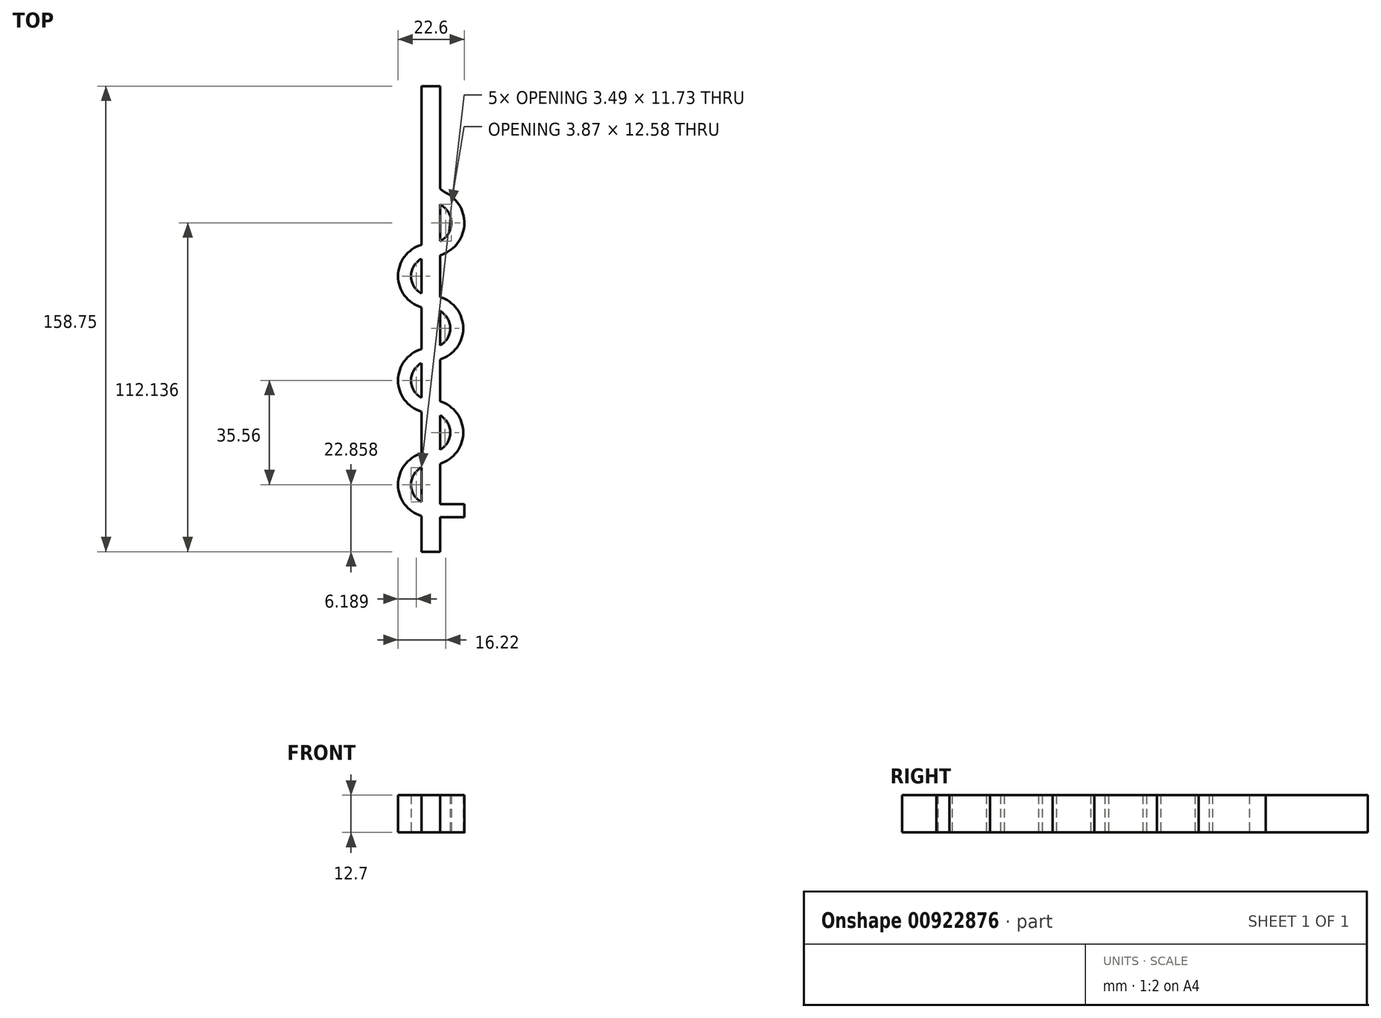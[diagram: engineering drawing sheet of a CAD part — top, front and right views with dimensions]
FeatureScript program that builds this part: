
annotation { "Feature Type Name" : "Feature", "Feature Type Description" : "" }
export const myFeature = defineFeature(function(context is Context, id is Id, definition is map)
    precondition{}
    {
        {
            var Q0;
            Q0=qCreatedBy(makeId("Top.planeOp"),FACE);
            var sketch = newSketch(context, id + "F0", { "sketchPlane" : qUnion([Q0])});
            skLineSegment(sketch, "E0.bottom", {"start": v(-3.18, 89.22) * mm, "end": v(3.17, 89.22) * mm});
            skLineSegment(sketch, "E0.top", {"start": v(-3.18, -69.53) * mm, "end": v(3.17, -69.53) * mm});
            skLineSegment(sketch, "E0.left", {"start": v(-3.18, 89.22) * mm, "end": v(-3.18, -69.53) * mm});
            skLineSegment(sketch, "E0.right", {"start": v(3.17, 89.22) * mm, "end": v(3.17, -69.53) * mm});
            skLineSegment(sketch, "E1", {"start": v(0, 96.84) * mm, "end": v(0, -80.96) * mm, "construction": true});
            skArc(sketch, "E2", {"start": v(0, -40) * mm, "mid": v(-6.67, -46.67) * mm, "end": v(0, -53.34) * mm});
            skArc(sketch, "E3", {"start": v(0, -35.56) * mm, "mid": v(-11.11, -46.67) * mm, "end": v(0, -57.79) * mm});
            skArc(sketch, "E4", {"start": v(0, 0) * mm, "mid": v(-11.11, -11.11) * mm, "end": v(0, -22.23) * mm});
            skArc(sketch, "E5", {"start": v(0, -4.45) * mm, "mid": v(-6.67, -11.11) * mm, "end": v(0, -17.78) * mm});
            skArc(sketch, "E6", {"start": v(0, 35.56) * mm, "mid": v(-11.11, 24.45) * mm, "end": v(0, 13.33) * mm});
            skArc(sketch, "E7", {"start": v(0, 31.12) * mm, "mid": v(-6.67, 24.45) * mm, "end": v(0, 17.78) * mm});
            skArc(sketch, "E8", {"start": v(0, 0) * mm, "mid": v(6.67, 6.67) * mm, "end": v(0, 13.33) * mm});
            skArc(sketch, "E9", {"start": v(0, -4.45) * mm, "mid": v(11.11, 6.67) * mm, "end": v(0, 17.78) * mm});
            skArc(sketch, "E10", {"start": v(0, -35.56) * mm, "mid": v(6.67, -28.9) * mm, "end": v(0, -22.23) * mm});
            skArc(sketch, "E11", {"start": v(0, -40) * mm, "mid": v(11.11, -28.9) * mm, "end": v(0, -17.78) * mm});
            skLineSegment(sketch, "E12", {"start": v(0, -57.78) * mm, "end": v(11.43, -57.78) * mm});
            skLineSegment(sketch, "E13", {"start": v(11.43, -57.78) * mm, "end": v(11.43, -53.34) * mm});
            skLineSegment(sketch, "E14", {"start": v(11.43, -53.34) * mm, "end": v(0, -53.34) * mm});
            skLineSegment(sketch, "E15", {"start": v(-22.23, 48.9) * mm, "end": v(3.17, 48.9) * mm, "construction": true});
            skArc(sketch, "E16", {"start": v(0, 35.56) * mm, "mid": v(6.85, 40.97) * mm, "end": v(3.17, 48.9) * mm});
            skArc(sketch, "E17", {"start": v(0, 31.12) * mm, "mid": v(11.18, 39.94) * mm, "end": v(5.18, 52.86) * mm});
            skArc(sketch, "E18", {"start": v(-3.18, 59.21) * mm, "mid": v(-1.46, 53.16) * mm, "end": v(3.17, 48.9) * mm});
            skArc(sketch, "E19", {"start": v(3.17, 54.37) * mm, "mid": v(4.1, 53.53) * mm, "end": v(5.18, 52.86) * mm});
            skSolve(sketch);
        }
        {
            var Q0;
            Q0 = qSketchRegion(id + "F0", true);
            extrude(context, id + "F1", {"entities" : qUnion([Q0]), "depth" : 12.7 * mm, "offsetDistance" : 25.4 * mm});
        }
    });
